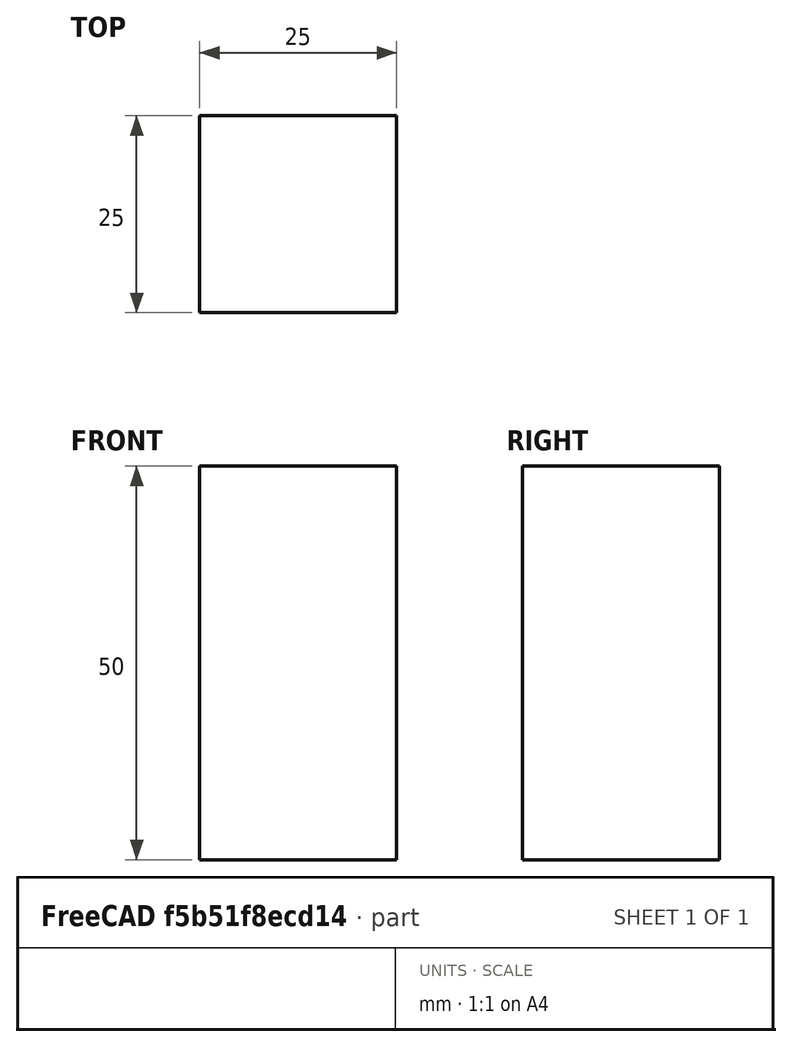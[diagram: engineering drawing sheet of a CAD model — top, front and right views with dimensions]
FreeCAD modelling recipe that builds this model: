
FCSTD DOCUMENT  (FreeCAD 0.15R4671 (Git))
Label: Square Bar 25 EN10059 S235JR
License: All rights reserved
LicenseURL: http://en.wikipedia.org/wiki/All_rights_reserved
objects: Sketcher::SketchObject×1, Part::Extrusion×1
note: 2 computed .brp shape members not serialized (recipe doc carries the construction recipe); baked Part::Feature solids carry a one-line shape summary decoded from their .brp

FEATURE [Sketcher::SketchObject] Sketch
  sketch-geometry (4):
    g0: LineSegment StartX=-12.5 StartY=-12.5 StartZ=0 EndX=12.5 EndY=-12.5 EndZ=0
    g1: LineSegment StartX=12.5 StartY=-12.5 StartZ=0 EndX=12.5 EndY=12.5 EndZ=0
    g2: LineSegment StartX=12.5 StartY=12.5 StartZ=0 EndX=-12.5 EndY=12.5 EndZ=0
    g3: LineSegment StartX=-12.5 StartY=12.5 StartZ=0 EndX=-12.5 EndY=-12.5 EndZ=0
  constraints (12):
    c: Coincident(g0,g1)
    c: Coincident(g1,g2)
    c: Coincident(g2,g3)
    c: Coincident(g3,g0)
    c: Horizontal(g0)
    c: Horizontal(g2)
    c: Vertical(g1)
    c: Vertical(g3)
    c: Symmetric(g1,g0,g-1)
    c: Symmetric(g2,g1,g-2)
    c: Equal(g1,g2)
    c: DistanceY(g1) = 25
FEATURE [Part::Extrusion] Extrude  label="Square Bar 25 EN10059 S235JR"
  Base = -> Sketch
  Dir = (0,0,50)
  Solid = true
